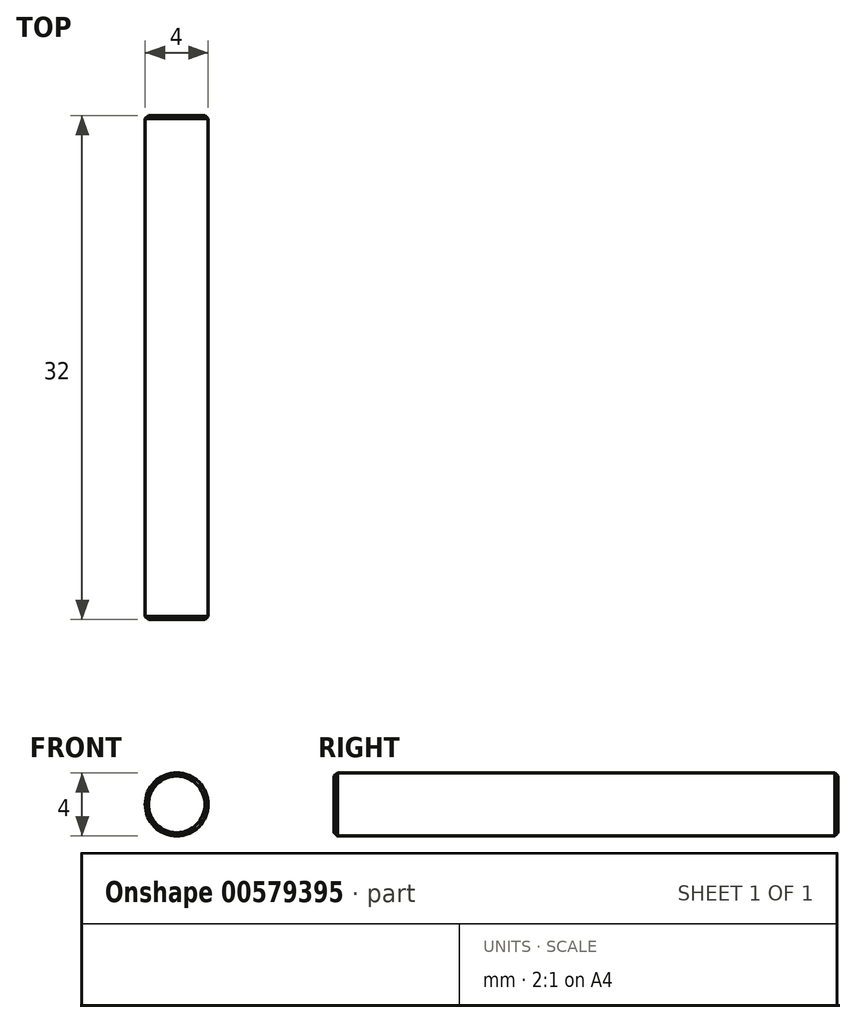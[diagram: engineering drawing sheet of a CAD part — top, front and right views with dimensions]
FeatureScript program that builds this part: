
annotation { "Feature Type Name" : "Feature", "Feature Type Description" : "" }
export const myFeature = defineFeature(function(context is Context, id is Id, definition is map)
    precondition{}
    {
        {
            var Q0;
            Q0=qCreatedBy(makeId("Front.planeOp"),FACE);
            var sketch = newSketch(context, id + "F0", { "sketchPlane" : qUnion([Q0])});
            skCircle(sketch, "E0", {"center": v(0, 0) * mm, "radius": 2 * mm});
            skSolve(sketch);
        }
        {
            var Q0;
            Q0 = qSketchRegion(id + "F0", true);
            extrude(context, id + "F1", {"entities" : qUnion([Q0]), "endBound" : BoundingType.SYMMETRIC, "depth" : 32 * mm, "offsetDistance" : 25 * mm});
        }
        {
            var Q0;
            Q0=makeQuery(id+"F1.opExtrude","CAP_EDGE",EDGE,{"disambiguationData":[OSD([sQuery(id+"F0.wireOp",EDGE,"E0")])],"isStart":false});
            var Q1;
            Q1=makeQuery(id+"F1.opExtrude","CAP_EDGE",EDGE,{"disambiguationData":[OSD([sQuery(id+"F0.wireOp",EDGE,"E0")])],"isStart":true});
            chamfer(context, id + "F2", {"entities" : qUnion([Q0, Q1]), "width" : .2 * mm, "tangentPropagation" : true});
        }
    });
